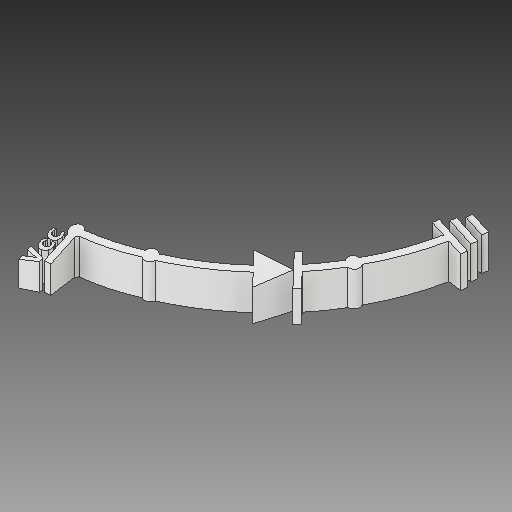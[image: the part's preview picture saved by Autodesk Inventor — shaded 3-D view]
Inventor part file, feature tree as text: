
AUTODESK INVENTOR PART (.ipt)
format: ipt  version: 2017 (Build 210142000, 142)  size: 352,768 bytes
history: native  units: in
note: dims shown in document units (in); Inventor stores cm internally (conversion verified against a paired STEP export)
features: sketch x3, extrude x2, revolve x1, projected_geometry x1
ambient origin geometry x8: Origin, YZ Plane, XZ Plane, XY Plane, X Axis, Y Axis, Z Axis, Center Point
bodies: Solid1 (feature_tree)
feature tree (7):
  revolve  "Revolution1"  [1 undecoded]
  extrude  "Extrusion1"  Depth=0.05in
  extrude  "Extrusion3"  Depth=0.075in
  sketch  "Sketch1"  dims[d0=0.8265in d1=0.175in]
  sketch  "Sketch2"  dims[d2=0.05in d3=0.1in]
  projected_geometry  "Projected Loop1"
  sketch  "Sketch4"  dims[d4=0.15in d5=0.275in d6=90.0deg d18=0.05in d26=0.05in d29=0.135in d31=0.025in d34=0.15in d35=0.05in d36=0.3in d39=0.135in d40=0.3in d42=0.025in d48=0.05in d49=0.3in d50=0.025in d52=0.3in d53=0.135in d54=0.025in d55=0.135in d56=0.05in d57=0.025in d59=0.15in d60=0.135in d61=0.1in d62=0.075in d63=0.025in d64=0.025in d65=0.025in d67=0.025in d69=0.1in d70=0.0in d74=0.0515in d75=0.0125in d77=0.0515in d78=0.025in d79=1.0in d80=0.0in]
note: 1 required parameter value undecoded (feature->parameter linkage not recoverable at this tier; creation-order binding heuristic only, values carry confidence <= 0.55)
